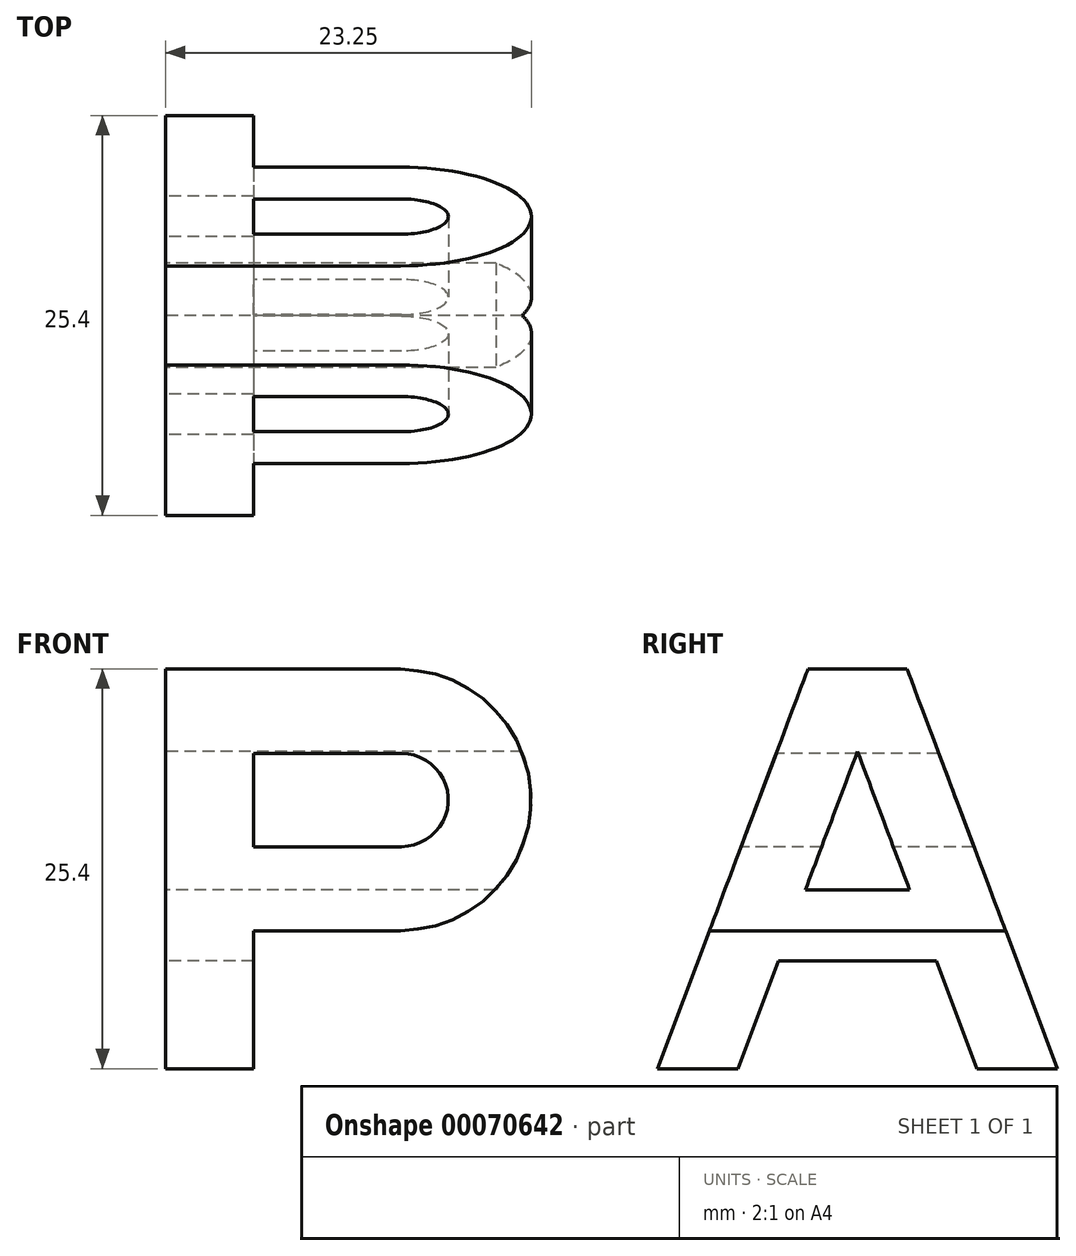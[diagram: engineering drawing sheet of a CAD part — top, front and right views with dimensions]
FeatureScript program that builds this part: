
annotation { "Feature Type Name" : "Feature", "Feature Type Description" : "" }
export const myFeature = defineFeature(function(context is Context, id is Id, definition is map)
    precondition{}
    {
        {
            var Q0;
            Q0=qCreatedBy(makeId("Top.planeOp"),FACE);
            var sketch = newSketch(context, id + "F0", { "sketchPlane" : qUnion([Q0])});
            skLineSegment(sketch, "E0.rect.bottom", {"start": v(12.7, 12.7) * mm, "end": v(-12.7, 12.7) * mm});
            skLineSegment(sketch, "E0.rect.top", {"start": v(12.7, -12.7) * mm, "end": v(-12.7, -12.7) * mm});
            skLineSegment(sketch, "E0.rect.left", {"start": v(12.7, 12.7) * mm, "end": v(12.7, -12.7) * mm});
            skLineSegment(sketch, "E0.rect.right", {"start": v(-12.7, 12.7) * mm, "end": v(-12.7, -12.7) * mm});
            skPoint(sketch, "E0.rect.middle", {"position": v(0, 0) * mm});
            skSolve(sketch);
        }
        {
            var Q0;
            Q0=makeQuery(id+"F0.imprint","IMPRINT",FACE,{"disambiguationData":[TD([[makeQuery(id+"F0.imprint","IMPRINT",EDGE,{"derivedFrom":sQuery(id+"F0.wireOp",EDGE,"E0.rect.bottom")}),1.0]])]});
            extrude(context, id + "F1", {"entities" : qUnion([Q0]), "depth" : 25.4 * mm});
        }
        {
            var Q0;
            Q0=makeQuery(id+"F1.opExtrude","CAP_FACE",FACE,{"disambiguationData":[OSD([sQuery(id+"F0.wireOp",EDGE,"E0.rect.bottom"),sQuery(id+"F0.wireOp",EDGE,"E0.rect.top"),sQuery(id+"F0.wireOp",EDGE,"E0.rect.left"),sQuery(id+"F0.wireOp",EDGE,"E0.rect.right")])],"isStart":false});
            var sketch = newSketch(context, id + "F2", { "sketchPlane" : qUnion([Q0])});
            skLineSegment(sketch, "E1", {"start": v(2.84, 0) * mm, "end": v(2.84, -3.59) * mm});
            skLineSegment(sketch, "E2", {"start": v(2.84, -3.59) * mm, "end": v(7.49, -3.59) * mm});
            skLineSegment(sketch, "E3", {"start": v(7.49, -3.59) * mm, "end": v(7.49, -7.9) * mm});
            skLineSegment(sketch, "E4", {"start": v(7.49, -7.9) * mm, "end": v(-6.95, -7.9) * mm});
            skLineSegment(sketch, "E5", {"start": v(-6.95, -7.9) * mm, "end": v(-6.95, 7.67) * mm});
            skLineSegment(sketch, "E6", {"start": v(12.7, 12.7) * mm, "end": v(-12.7, 12.7) * mm});
            skLineSegment(sketch, "E7", {"start": v(-12.7, 12.7) * mm, "end": v(-12.7, -12.7) * mm});
            skLineSegment(sketch, "E8", {"start": v(-12.7, -12.7) * mm, "end": v(12.7, -12.7) * mm});
            skLineSegment(sketch, "E9", {"start": v(12.7, -12.7) * mm, "end": v(12.7, 1.96) * mm});
            skLineSegment(sketch, "E10", {"start": v(12.7, 1.96) * mm, "end": v(2.84, 0) * mm});
            skLineSegment(sketch, "E11", {"start": v(-6.95, 7.67) * mm, "end": v(9.36, 7.67) * mm});
            skLineSegment(sketch, "E12", {"start": v(9.36, 7.67) * mm, "end": v(12.7, 12.7) * mm});
            skSolve(sketch);
        }
        {
            var Q0;
            Q0=makeQuery(id+"F1.opExtrude","SWEPT_FACE",FACE,{"disambiguationData":[OSD([sQuery(id+"F0.wireOp",EDGE,"E0.rect.right")])]});
            var sketch = newSketch(context, id + "F3", { "sketchPlane" : qUnion([Q0])});
            skLineSegment(sketch, "E13", {"start": v(0, 0) * mm, "end": v(0, 25.4) * mm, "construction": true});
            skLineSegment(sketch, "E14", {"start": v(0, 25.4) * mm, "end": v(-3.14, 25.4) * mm});
            skLineSegment(sketch, "E15", {"start": v(-3.14, 25.4) * mm, "end": v(-12.7, 0) * mm});
            skLineSegment(sketch, "E16", {"start": v(-12.7, 0) * mm, "end": v(-7.58, 0) * mm});
            skLineSegment(sketch, "E17", {"start": v(-7.58, 0) * mm, "end": v(-5.01, 6.83) * mm});
            skLineSegment(sketch, "E18", {"start": v(-5.01, 6.83) * mm, "end": v(0, 6.83) * mm});
            skLineSegment(sketch, "E19", {"start": v(0, 20.15) * mm, "end": v(-3.3, 11.36) * mm});
            skLineSegment(sketch, "E20", {"start": v(-3.3, 11.36) * mm, "end": v(0, 11.36) * mm});
            skLineSegment(sketch, "E21.MirrorCS", {"start": v(3.3, 11.36) * mm, "end": v(0, 11.36) * mm});
            skLineSegment(sketch, "E22.MirrorCS", {"start": v(0, 20.15) * mm, "end": v(3.3, 11.36) * mm});
            skLineSegment(sketch, "E23.MirrorCS", {"start": v(5.01, 6.83) * mm, "end": v(0, 6.83) * mm});
            skLineSegment(sketch, "E24.MirrorCS", {"start": v(7.58, 0) * mm, "end": v(5.01, 6.83) * mm});
            skLineSegment(sketch, "E25.MirrorCS", {"start": v(0, 25.4) * mm, "end": v(3.14, 25.4) * mm});
            skLineSegment(sketch, "E26.MirrorCS", {"start": v(12.7, 0) * mm, "end": v(7.58, 0) * mm});
            skLineSegment(sketch, "E27.MirrorCS", {"start": v(3.14, 25.4) * mm, "end": v(12.7, 0) * mm});
            skSolve(sketch);
        }
        {
            var Q0;
            Q0=makeQuery(id+"F1.opExtrude","SWEPT_FACE",FACE,{"disambiguationData":[OSD([sQuery(id+"F0.wireOp",EDGE,"E0.rect.top")])]});
            var sketch = newSketch(context, id + "F4", { "sketchPlane" : qUnion([Q0])});
            skLineSegment(sketch, "E28", {"start": v(-12.7, 25.4) * mm, "end": v(-12.7, 0) * mm});
            skLineSegment(sketch, "E29", {"start": v(-12.7, 0) * mm, "end": v(-7.11, 0) * mm});
            skLineSegment(sketch, "E30", {"start": v(-7.11, 0) * mm, "end": v(-7.11, 8.74) * mm});
            skLineSegment(sketch, "E31", {"start": v(-12.7, 0) * mm, "end": v(12.7, 25.4) * mm, "construction": true});
            skPoint(sketch, "E32", {"position": v(0, 12.7) * mm});
            skLineSegment(sketch, "E33.1.4", {"start": v(-7.11, 25.4) * mm, "end": v(-12.7, 25.4) * mm});
            skLineSegment(sketch, "E34", {"start": v(-7.11, 25.4) * mm, "end": v(2.22, 25.4) * mm});
            skLineSegment(sketch, "E35", {"start": v(-7.11, 8.74) * mm, "end": v(2.22, 8.74) * mm});
            skLineSegment(sketch, "E36", {"start": v(-7.11, 14.1) * mm, "end": v(-7.11, 20.04) * mm});
            skLineSegment(sketch, "E37", {"start": v(-7.11, 20.04) * mm, "end": v(2.3, 20.04) * mm});
            skLineSegment(sketch, "E38", {"start": v(-7.11, 14.1) * mm, "end": v(2.3, 14.1) * mm});
            skCircle(sketch, "E39", {"center": v(2.3, 17.07) * mm, "radius": 2.97 * mm});
            skPoint(sketch, "E39.centerSnap0", {"position": v(-7.11, 17.07) * mm});
            skCircle(sketch, "E40", {"center": v(2.22, 17.07) * mm, "radius": 8.33 * mm});
            skSolve(sketch);
        }
        {
            var Q0;
            Q0=makeQuery(id+"F3.imprint","IMPRINT",FACE,{"disambiguationData":[TD([[makeQuery(id+"F3.imprint","IMPRINT",EDGE,{"derivedFrom":sQuery(id+"F3.wireOp",EDGE,"E14")}),-1.0]])]});
            extrude(context, id + "F5", {"entities" : qUnion([Q0]), "operationType" : NewBodyOperationType.INTERSECT, "endBound" : BoundingType.THROUGH_ALL, "oppositeDirection" : true, "depth" : 25.4 * mm});
        }
        {
            var Q0;
            Q0=makeQuery(id+"F4.imprint","IMPRINT",FACE,{"disambiguationData":[TD([[makeQuery(id+"F4.imprint","IMPRINT",EDGE,{"derivedFrom":sQuery(id+"F4.wireOp",EDGE,"E28")}),1.0]])]});
            var Q1;
            {var subQ2=sQuery(id+"F4.wireOp",EDGE,"E37");var subQ4=sQuery(id+"F4.wireOp",EDGE,"E39");var subQ5=makeQuery(id+"F4.imprint","INTERSECT",VERTEX,{"derivedFrom":[subQ2,subQ4]});Q1=makeQuery(id+"F4.imprint","IMPRINT",FACE,{"disambiguationData":[TD([[makeQuery(id+"F4.imprint","IMPRINT",EDGE,{"disambiguationData":[TD([[subQ5,1.0]])],"derivedFrom":subQ2}),1.0]])]});}
            extrude(context, id + "F6", {"entities" : qUnion([Q0, Q1]), "operationType" : NewBodyOperationType.INTERSECT, "endBound" : BoundingType.THROUGH_ALL, "oppositeDirection" : true, "depth" : 25.4 * mm});
        }
    });
